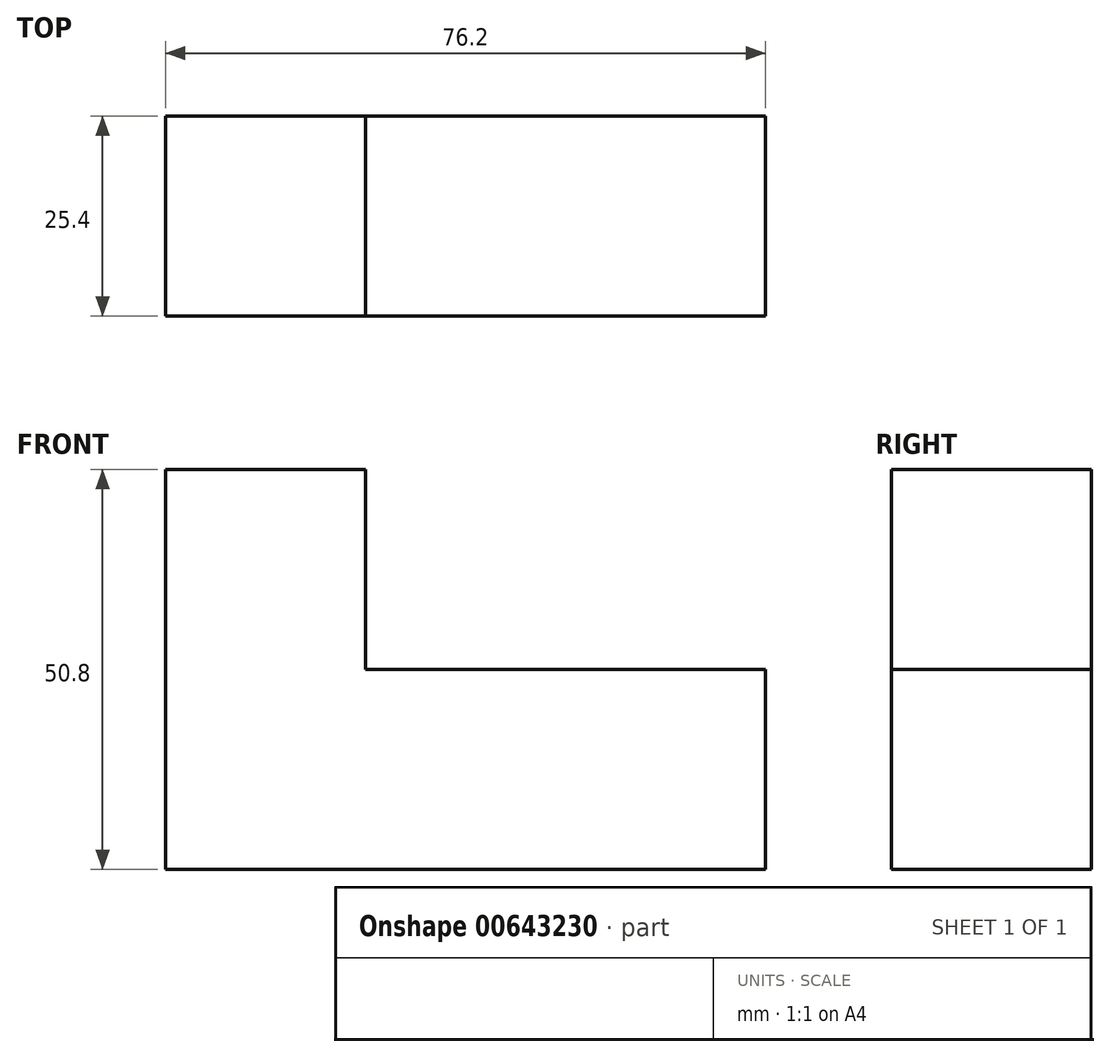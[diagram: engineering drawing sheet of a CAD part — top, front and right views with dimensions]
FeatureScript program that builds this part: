
annotation { "Feature Type Name" : "Feature", "Feature Type Description" : "" }
export const myFeature = defineFeature(function(context is Context, id is Id, definition is map)
    precondition{}
    {
        {
            var Q0;
            Q0=qCreatedBy(makeId("Front.planeOp"),FACE);
            var sketch = newSketch(context, id + "F0", { "sketchPlane" : qUnion([Q0])});
            skLineSegment(sketch, "E0.bottom", {"start": v(0, 0) * mm, "end": v(25.4, 0) * mm});
            skLineSegment(sketch, "E0.top", {"start": v(0, 25.4) * mm, "end": v(25.4, 25.4) * mm});
            skLineSegment(sketch, "E0.left", {"start": v(0, 0) * mm, "end": v(0, 25.4) * mm});
            skLineSegment(sketch, "E0.right", {"start": v(25.4, 0) * mm, "end": v(25.4, 25.4) * mm});
            skLineSegment(sketch, "E1.bottom", {"start": v(25.4, 25.4) * mm, "end": v(50.8, 25.4) * mm});
            skLineSegment(sketch, "E1.top", {"start": v(25.4, 0) * mm, "end": v(50.8, 0) * mm});
            skLineSegment(sketch, "E1.left", {"start": v(25.4, 25.4) * mm, "end": v(25.4, 0) * mm});
            skLineSegment(sketch, "E1.right", {"start": v(50.8, 25.4) * mm, "end": v(50.8, 0) * mm});
            skLineSegment(sketch, "E2.bottom", {"start": v(50.8, 25.4) * mm, "end": v(76.2, 25.4) * mm});
            skLineSegment(sketch, "E2.top", {"start": v(50.8, 0) * mm, "end": v(76.2, 0) * mm});
            skLineSegment(sketch, "E2.right", {"start": v(76.2, 25.4) * mm, "end": v(76.2, 0) * mm});
            skLineSegment(sketch, "E3.top", {"start": v(0, 50.8) * mm, "end": v(25.4, 50.8) * mm});
            skLineSegment(sketch, "E3.left", {"start": v(0, 25.4) * mm, "end": v(0, 50.8) * mm});
            skLineSegment(sketch, "E3.right", {"start": v(25.4, 25.4) * mm, "end": v(25.4, 50.8) * mm});
            skSolve(sketch);
        }
        {
            var Q0;
            Q0=makeQuery(id+"F0.imprint","IMPRINT",FACE,{"disambiguationData":[TD([[makeQuery(id+"F0.imprint","IMPRINT",EDGE,{"derivedFrom":sQuery(id+"F0.wireOp",EDGE,"E0.top")}),1.0]])]});
            var Q1;
            Q1=makeQuery(id+"F0.imprint","IMPRINT",FACE,{"disambiguationData":[TD([[makeQuery(id+"F0.imprint","IMPRINT",EDGE,{"derivedFrom":sQuery(id+"F0.wireOp",EDGE,"E0.bottom")}),1.0]])]});
            var Q2;
            Q2=makeQuery(id+"F0.imprint","IMPRINT",FACE,{"disambiguationData":[TD([[makeQuery(id+"F0.imprint","IMPRINT",EDGE,{"derivedFrom":sQuery(id+"F0.wireOp",EDGE,"E1.bottom")}),-1.0]])]});
            var Q3;
            Q3=makeQuery(id+"F0.imprint","IMPRINT",FACE,{"disambiguationData":[TD([[makeQuery(id+"F0.imprint","IMPRINT",EDGE,{"derivedFrom":sQuery(id+"F0.wireOp",EDGE,"E2.bottom")}),-1.0]])]});
            extrude(context, id + "F1", {"entities" : qUnion([Q0, Q1, Q2, Q3]), "depth" : 25.4 * mm, "offsetDistance" : 25.4 * mm});
        }
    });
